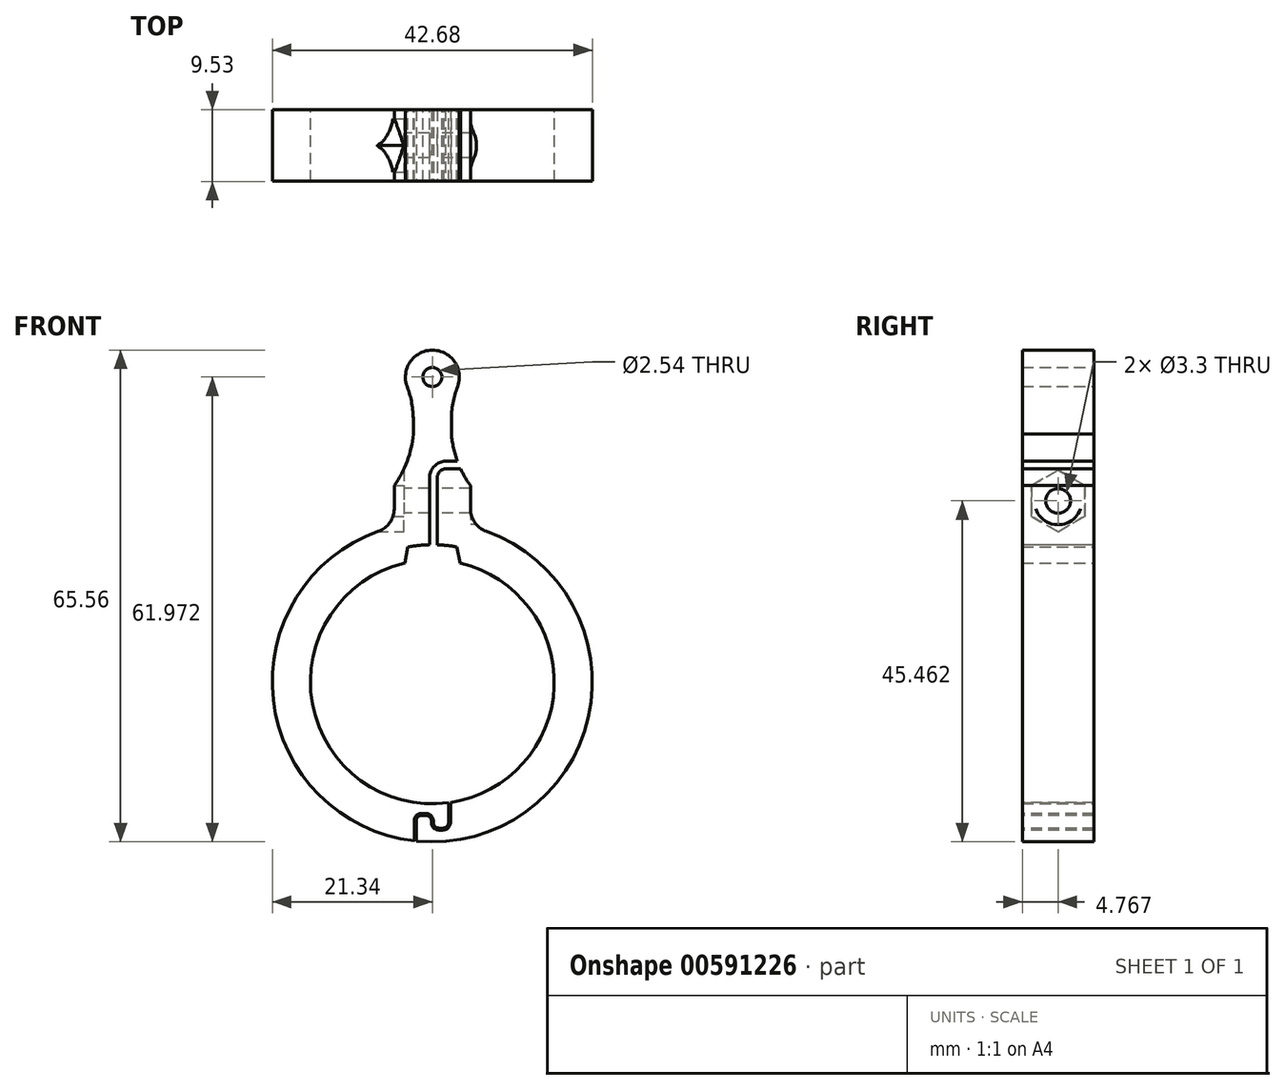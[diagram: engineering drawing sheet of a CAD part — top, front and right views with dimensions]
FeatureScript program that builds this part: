
annotation { "Feature Type Name" : "Feature", "Feature Type Description" : "" }
export const myFeature = defineFeature(function(context is Context, id is Id, definition is map)
    precondition{}
    {
        {
            var Q0;
            Q0=qCreatedBy(makeId("Front.planeOp"),FACE);
            var sketch = newSketch(context, id + "F0", { "sketchPlane" : qUnion([Q0])});
            skArc(sketch, "E0", {"start": v(-3.7, 4.38) * mm, "mid": v(0, -27.7) * mm, "end": v(3.7, 4.38) * mm});
            skArc(sketch, "E1", {"start": v(-2.54, 23.43) * mm, "mid": v(-2.75, 25.71) * mm, "end": v(-3.36, 27.92) * mm});
            skArc(sketch, "E2", {"start": v(3.36, 27.92) * mm, "mid": v(2.75, 25.71) * mm, "end": v(2.54, 23.43) * mm});
            skArc(sketch, "E3", {"start": v(3.36, 27.92) * mm, "mid": v(0, 32.78) * mm, "end": v(-3.36, 27.92) * mm});
            skArc(sketch, "E4", {"start": v(-7.19, 8.64) * mm, "mid": v(-5.66, 9.8) * mm, "end": v(-5.08, 11.63) * mm});
            skArc(sketch, "E5", {"start": v(5.08, 11.63) * mm, "mid": v(5.66, 9.8) * mm, "end": v(7.19, 8.64) * mm});
            skArc(sketch, "E6", {"start": v(-7.19, 8.64) * mm, "mid": v(0, -32.78) * mm, "end": v(7.19, 8.64) * mm});
            skLineSegment(sketch, "E7", {"start": v(-5.08, 11.63) * mm, "end": v(-5.08, 14.73) * mm});
            skLineSegment(sketch, "E8", {"start": v(5.08, 11.63) * mm, "end": v(5.08, 14.73) * mm});
            skLineSegment(sketch, "E9", {"start": v(-3.7, 4.38) * mm, "end": v(-3.26, 6.54) * mm});
            skLineSegment(sketch, "E10", {"start": v(3.7, 4.38) * mm, "end": v(3.26, 6.54) * mm});
            skLineSegment(sketch, "E11", {"start": v(-10.67, 12.68) * mm, "end": v(10.41, 12.68) * mm, "construction": true});
            skArc(sketch, "E12", {"start": v(3.26, 6.54) * mm, "mid": v(1.83, 6.75) * mm, "end": v(0.38, 6.84) * mm});
            skArc(sketch, "E13", {"start": v(-0.38, 6.84) * mm, "mid": v(-1.83, 6.75) * mm, "end": v(-3.26, 6.54) * mm});
            skLineSegment(sketch, "E14", {"start": v(-0.38, 6.84) * mm, "end": v(-0.38, 15.7) * mm});
            skCircle(sketch, "E15", {"center": v(0, 29.2) * mm, "radius": 1.27 * mm});
            skArc(sketch, "E16", {"start": v(-5.08, 14.71) * mm, "mid": v(-3.35, 17.97) * mm, "end": v(-2.54, 21.57) * mm});
            skLineSegment(sketch, "E17", {"start": v(-2.54, 21.57) * mm, "end": v(-2.54, 23.43) * mm});
            skLineSegment(sketch, "E18", {"start": v(2.54, 23.43) * mm, "end": v(2.54, 21.57) * mm});
            skLineSegment(sketch, "E19", {"start": v(1.56, 17.97) * mm, "end": v(3.35, 17.97) * mm});
            skArc(sketch, "E20", {"start": v(1.58, 17.97) * mm, "mid": v(0.18, 17.2) * mm, "end": v(-0.38, 15.7) * mm});
            skLineSegment(sketch, "E21", {"start": v(0.38, 6.84) * mm, "end": v(0.38, 15.7) * mm});
            skArc(sketch, "E22", {"start": v(1.69, 17.21) * mm, "mid": v(0.75, 16.7) * mm, "end": v(0.38, 15.7) * mm});
            skLineSegment(sketch, "E23", {"start": v(1.69, 17.21) * mm, "end": v(3.65, 17.21) * mm});
            skArc(sketch, "E24", {"start": v(3.65, 17.21) * mm, "mid": v(4.3, 15.93) * mm, "end": v(5.08, 14.71) * mm});
            skArc(sketch, "E25", {"start": v(2.54, 21.57) * mm, "mid": v(2.82, 19.74) * mm, "end": v(3.35, 17.97) * mm});
            skSolve(sketch);
        }
        {
            var Q0;
            Q0 = qSketchRegion(id + "F0", true);
            extrude(context, id + "F1", {"entities" : qUnion([Q0]), "depth" : 9.52 * mm, "offsetDistance" : 25.4 * mm});
        }
        {
            var Q0;
            Q0=makeQuery(id+"F1.opExtrude","SWEPT_FACE",FACE,{"disambiguationData":[OSD([sQuery(id+"F0.wireOp",EDGE,"E7")])]});
            var sketch = newSketch(context, id + "F2", { "sketchPlane" : qUnion([Q0])});
            skCircle(sketch, "E26", {"center": v(4.76, 12.68) * mm, "radius": 1.65 * mm});
            skLineSegment(sketch, "E27", {"start": v(9.52, 12.68) * mm, "end": v(0, 12.68) * mm, "construction": true});
            skSolve(sketch);
        }
        {
            var Q0;
            Q0 = qSketchRegion(id + "F2", true);
            extrude(context, id + "F3", {"entities" : qUnion([Q0]), "operationType" : NewBodyOperationType.REMOVE, "endBound" : BoundingType.THROUGH_ALL, "oppositeDirection" : true, "depth" : 25.4 * mm, "offsetDistance" : 25.4 * mm});
        }
        {
            var Q0;
            Q0=makeQuery(id+"F1.opExtrude","SWEPT_FACE",FACE,{"disambiguationData":[OSD([sQuery(id+"F0.wireOp",EDGE,"E7")])]});
            var sketch = newSketch(context, id + "F4", { "sketchPlane" : qUnion([Q0])});
            skCircle(sketch, "E28.cCircle", {"center": v(4.76, 12.68) * mm, "radius": 3.56 * mm, "construction": true});
            skLineSegment(sketch, "E28.0", {"start": v(8.32, 14.73) * mm, "end": v(8.32, 10.63) * mm});
            skLineSegment(sketch, "E28.1", {"start": v(8.32, 10.63) * mm, "end": v(4.76, 8.58) * mm});
            skLineSegment(sketch, "E28.2", {"start": v(4.76, 8.58) * mm, "end": v(1.2, 10.63) * mm});
            skLineSegment(sketch, "E28.3", {"start": v(1.2, 10.63) * mm, "end": v(1.2, 14.73) * mm});
            skLineSegment(sketch, "E28.4", {"start": v(1.2, 14.73) * mm, "end": v(4.76, 16.79) * mm});
            skLineSegment(sketch, "E28.5", {"start": v(4.76, 16.79) * mm, "end": v(8.32, 14.73) * mm});
            skPoint(sketch, "E28.0.midPoint", {"position": v(8.32, 12.68) * mm});
            skSolve(sketch);
        }
        {
            var Q0;
            Q0 = qSketchRegion(id + "F4", true);
            extrude(context, id + "F5", {"entities" : qUnion([Q0]), "operationType" : NewBodyOperationType.REMOVE, "endBound" : BoundingType.THROUGH_ALL, "depth" : 25.4 * mm, "offsetDistance" : 25.4 * mm, "hasSecondDirection" : true, "secondDirectionOppositeDirection" : true, "secondDirectionDepth" : 1.27 * mm});
        }
        {
            var Q0;
            Q0=makeQuery(id+"F1.opExtrude","SWEPT_FACE",FACE,{"disambiguationData":[OSD([sQuery(id+"F0.wireOp",EDGE,"E8")])]});
            var sketch = newSketch(context, id + "F6", { "sketchPlane" : qUnion([Q0])});
            skCircle(sketch, "E29", {"center": v(-4.76, 12.68) * mm, "radius": 3.18 * mm});
            skSolve(sketch);
        }
        {
            var Q0;
            Q0 = qSketchRegion(id + "F6", true);
            extrude(context, id + "F7", {"entities" : qUnion([Q0]), "operationType" : NewBodyOperationType.REMOVE, "endBound" : BoundingType.THROUGH_ALL, "depth" : 25.4 * mm, "offsetDistance" : 25.4 * mm});
        }
        {
            var Q0;
            Q0=makeQuery(id+"F0.imprint","IMPRINT",FACE,{"disambiguationData":[TD([[makeQuery(id+"F0.imprint","IMPRINT",EDGE,{"derivedFrom":sQuery(id+"F0.wireOp",EDGE,"E0")}),-1.0]])]});
            var sketch = newSketch(context, id + "F8", { "sketchPlane" : qUnion([Q0])});
            skArc(sketch, "E30", {"start": v(-7.19, 8.64) * mm, "mid": v(0, -28.97) * mm, "end": v(7.19, 8.64) * mm});
            skPoint(sketch, "E30.first.point", {"position": v(7.19, 8.64) * mm});
            skPoint(sketch, "E30.second.point", {"position": v(-7.19, 8.64) * mm});
            skPoint(sketch, "E30.third.point", {"position": v(0, -28.97) * mm});
            skPoint(sketch, "E31", {"position": v(0, -27.95) * mm});
            skArc(sketch, "E32.0", {"start": v(-7.19, 8.64) * mm, "mid": v(0, -32.78) * mm, "end": v(7.19, 8.64) * mm});
            skSolve(sketch);
        }
        {
            var Q0;
            Q0=makeQuery(id+"F1.opExtrude","CAP_FACE",FACE,{"disambiguationData":[OSD([sQuery(id+"F0.wireOp",EDGE,"E0"),sQuery(id+"F0.wireOp",EDGE,"E1"),sQuery(id+"F0.wireOp",EDGE,"E2"),sQuery(id+"F0.wireOp",EDGE,"E3"),sQuery(id+"F0.wireOp",EDGE,"E4"),sQuery(id+"F0.wireOp",EDGE,"E5"),sQuery(id+"F0.wireOp",EDGE,"E6"),sQuery(id+"F0.wireOp",EDGE,"E7"),sQuery(id+"F0.wireOp",EDGE,"E8"),sQuery(id+"F0.wireOp",EDGE,"E9"),sQuery(id+"F0.wireOp",EDGE,"E10"),sQuery(id+"F0.wireOp",EDGE,"E12"),sQuery(id+"F0.wireOp",EDGE,"E13"),sQuery(id+"F0.wireOp",EDGE,"E14"),sQuery(id+"F0.wireOp",EDGE,"E15"),sQuery(id+"F0.wireOp",EDGE,"E16"),sQuery(id+"F0.wireOp",EDGE,"E17"),sQuery(id+"F0.wireOp",EDGE,"E18"),sQuery(id+"F0.wireOp",EDGE,"E19"),sQuery(id+"F0.wireOp",EDGE,"E20"),sQuery(id+"F0.wireOp",EDGE,"E21"),sQuery(id+"F0.wireOp",EDGE,"E22"),sQuery(id+"F0.wireOp",EDGE,"E23"),sQuery(id+"F0.wireOp",EDGE,"E24"),sQuery(id+"F0.wireOp",EDGE,"E25")])],"isStart":false});
            var sketch = newSketch(context, id + "F9", { "sketchPlane" : qUnion([Q0])});
            skLineSegment(sketch, "E33", {"start": v(2.41, -27.52) * mm, "end": v(2.41, -30.2) * mm});
            skLineSegment(sketch, "E34", {"start": v(1.4, -31.2) * mm, "end": v(0.89, -31.2) * mm});
            skLineSegment(sketch, "E35", {"start": v(-0.13, -30.2) * mm, "end": v(-0.13, -30) * mm});
            skLineSegment(sketch, "E36", {"start": v(-0.89, -29.25) * mm, "end": v(-1.4, -29.25) * mm});
            skLineSegment(sketch, "E37", {"start": v(-2.16, -30) * mm, "end": v(-2.16, -32.67) * mm});
            skLineSegment(sketch, "E38.0", {"start": v(-2.41, -30) * mm, "end": v(-2.41, -32.67) * mm});
            skLineSegment(sketch, "E38.1", {"start": v(2.16, -27.52) * mm, "end": v(2.16, -30.2) * mm});
            skLineSegment(sketch, "E38.2", {"start": v(1.4, -30.95) * mm, "end": v(0.89, -30.95) * mm});
            skLineSegment(sketch, "E38.3", {"start": v(0.13, -30.2) * mm, "end": v(0.13, -30) * mm});
            skLineSegment(sketch, "E38.4", {"start": v(-0.89, -29) * mm, "end": v(-1.4, -29) * mm});
            skLineSegment(sketch, "E39", {"start": v(2.16, -27.52) * mm, "end": v(2.41, -27.52) * mm});
            skLineSegment(sketch, "E40", {"start": v(-2.16, -32.67) * mm, "end": v(-2.41, -32.67) * mm});
            skLineSegment(sketch, "E41", {"start": v(-0.13, -30.23) * mm, "end": v(0.13, -29.97) * mm, "construction": true});
            skLineSegment(sketch, "E42", {"start": v(0, -27.7) * mm, "end": v(0, -30.1) * mm, "construction": true});
            skPoint(sketch, "E43.visualSharp", {"position": v(-2.41, -29) * mm});
            skArc(sketch, "E43.filletArc", {"start": v(-1.4, -29) * mm, "mid": v(-2.12, -29.29) * mm, "end": v(-2.41, -30) * mm});
            skPoint(sketch, "E44.visualSharp", {"position": v(-0.13, -31.2) * mm});
            skArc(sketch, "E44.filletArc", {"start": v(-0.13, -30.2) * mm, "mid": v(0.17, -30.9) * mm, "end": v(0.89, -31.2) * mm});
            skPoint(sketch, "E45.visualSharp", {"position": v(2.41, -31.2) * mm});
            skArc(sketch, "E45.filletArc", {"start": v(1.4, -31.2) * mm, "mid": v(2.12, -30.9) * mm, "end": v(2.41, -30.2) * mm});
            skPoint(sketch, "E46.visualSharp", {"position": v(-2.16, -29.25) * mm});
            skArc(sketch, "E46.filletArc", {"start": v(-1.4, -29.25) * mm, "mid": v(-1.94, -29.47) * mm, "end": v(-2.16, -30) * mm});
            skPoint(sketch, "E47.visualSharp", {"position": v(-0.13, -29.25) * mm});
            skArc(sketch, "E47.filletArc", {"start": v(-0.13, -30) * mm, "mid": v(-0.35, -29.47) * mm, "end": v(-0.89, -29.25) * mm});
            skPoint(sketch, "E48.visualSharp", {"position": v(0.13, -30.95) * mm});
            skArc(sketch, "E48.filletArc", {"start": v(0.13, -30.2) * mm, "mid": v(0.35, -30.73) * mm, "end": v(0.89, -30.95) * mm});
            skPoint(sketch, "E49.visualSharp", {"position": v(2.16, -30.95) * mm});
            skArc(sketch, "E49.filletArc", {"start": v(1.4, -30.95) * mm, "mid": v(1.94, -30.73) * mm, "end": v(2.16, -30.2) * mm});
            skPoint(sketch, "E50.visualSharp", {"position": v(0.13, -29) * mm});
            skArc(sketch, "E50.filletArc", {"start": v(0.13, -30) * mm, "mid": v(-0.17, -29.29) * mm, "end": v(-0.89, -29) * mm});
            skSolve(sketch);
        }
        {
            var Q0;
            Q0 = qSketchRegion(id + "F9", true);
            extrude(context, id + "F10", {"entities" : qUnion([Q0]), "operationType" : NewBodyOperationType.REMOVE, "endBound" : BoundingType.THROUGH_ALL, "oppositeDirection" : true, "depth" : 25.4 * mm, "offsetDistance" : 25.4 * mm});
        }
        {
            var Q0;
            {var subQ0=sQuery(id+"F0.wireOp",EDGE,"E24");var subQ1=sQuery(id+"F0.wireOp",EDGE,"E23");var subQ2=sQuery(id+"F0.wireOp",EDGE,"E12");var subQ3=sQuery(id+"F0.wireOp",EDGE,"E22");var subQ4=sQuery(id+"F0.wireOp",EDGE,"E0");var subQ5=sQuery(id+"F0.wireOp",EDGE,"E10");var subQ6=sQuery(id+"F0.wireOp",EDGE,"E21");var subQ7=sQuery(id+"F0.wireOp",EDGE,"E8");var subQ8=sQuery(id+"F0.wireOp",EDGE,"E5");var subQ9=sQuery(id+"F0.wireOp",EDGE,"E6");Q0=makeQuery(id+"F10.boolean.opBoolean","SPLIT",FACE,{"disambiguationData":[TD([makeQuery(id+"F1.opExtrude","SWEPT_FACE",FACE,{"disambiguationData":[OSD([subQ8])]})])],"derivedFrom":makeQuery(id+"F1.opExtrude","CAP_FACE",FACE,{"disambiguationData":[OSD([subQ4,sQuery(id+"F0.wireOp",EDGE,"E1"),sQuery(id+"F0.wireOp",EDGE,"E2"),sQuery(id+"F0.wireOp",EDGE,"E3"),sQuery(id+"F0.wireOp",EDGE,"E4"),subQ8,subQ9,sQuery(id+"F0.wireOp",EDGE,"E7"),subQ7,sQuery(id+"F0.wireOp",EDGE,"E9"),subQ5,subQ2,sQuery(id+"F0.wireOp",EDGE,"E13"),sQuery(id+"F0.wireOp",EDGE,"E14"),sQuery(id+"F0.wireOp",EDGE,"E15"),sQuery(id+"F0.wireOp",EDGE,"E16"),sQuery(id+"F0.wireOp",EDGE,"E17"),sQuery(id+"F0.wireOp",EDGE,"E18"),sQuery(id+"F0.wireOp",EDGE,"E19"),sQuery(id+"F0.wireOp",EDGE,"E20"),subQ6,subQ3,subQ1,subQ0,sQuery(id+"F0.wireOp",EDGE,"E25")])],"isStart":false})});}
            var sketch = newSketch(context, id + "F11", { "sketchPlane" : qUnion([Q0])});
            skLineSegment(sketch, "E51.0", {"start": v(1.7, 16.96) * mm, "end": v(3.77, 16.96) * mm});
            skArc(sketch, "E51.1", {"start": v(1.7, 16.96) * mm, "mid": v(0.94, 16.53) * mm, "end": v(0.63, 15.7) * mm});
            skLineSegment(sketch, "E51.2", {"start": v(0.63, 6.83) * mm, "end": v(0.63, 15.7) * mm});
            skLineSegment(sketch, "E52.0", {"start": v(1.69, 17.21) * mm, "end": v(3.65, 17.21) * mm});
            skArc(sketch, "E52.1", {"start": v(1.69, 17.21) * mm, "mid": v(0.75, 16.7) * mm, "end": v(0.38, 15.7) * mm});
            skLineSegment(sketch, "E52.2", {"start": v(0.38, 6.84) * mm, "end": v(0.38, 15.7) * mm});
            skArc(sketch, "E53.0", {"start": v(3.65, 17.21) * mm, "mid": v(3.71, 17.08) * mm, "end": v(3.77, 16.96) * mm});
            skArc(sketch, "E53.1", {"start": v(0.63, 6.83) * mm, "mid": v(0.5, 6.83) * mm, "end": v(0.38, 6.84) * mm});
            skPoint(sketch, "E54.orphan", {"position": v(5.08, 14.71) * mm});
            skPoint(sketch, "E55.orphan", {"position": v(3.26, 6.54) * mm});
            skSolve(sketch);
        }
        {
            var Q0;
            Q0 = qSketchRegion(id + "F11", true);
            extrude(context, id + "F12", {"entities" : qUnion([Q0]), "operationType" : NewBodyOperationType.REMOVE, "endBound" : BoundingType.THROUGH_ALL, "oppositeDirection" : true, "depth" : 25.4 * mm, "offsetDistance" : 25.4 * mm});
        }
    });
